# Revit family: Practibox_S_flush_mounting_cabinet_8_modules_réf_134008_to_134178
name_source: partatom
category: Equipement électrique
revit_build: Autodesk Revit 2018 (Build: 20170223_1515(x64)
units: mm (PartAtom-declared; Revit-internal decimal feet)

## family parameters
Basée sur le plan de construction = Non
Configuration du panneau = Deux colonnes, circuits au sein
Cote de connecteur circulaire = Utiliser le diamètre
Couper avec des vides une fois chargée = Non
Numéro OmniClass = 23.80.30.11.17
Partagée = Non
Point de calcul de pièce = Non
Titre OmniClass = Distribution Boards and Control Panels
Toujours verticalement = Oui
Type d'élément = Tableau de raccordement

## types (8) — shared parameters
Fabricant = "Legrand"
General Conditions of Use = https://export.legrand.com
Ina = 63 A
URL = www.legrand.com
depth = 100 mm  [stored 0.328084 ft]
height = 225 mm  [stored 0.738189 ft]
size = 8 modules
width = 184 mm  [stored 0.603675 ft]

## per-type parameters (varying)
| type | Terminal block E | Terminal block N | door transparent | door white |
| Practibox_S_flush_mounting_cabinet_8_modules_134148 | 6 connections Icc 6kA | 6 connections Icc 6kA | Non | Oui |
| Practibox_S_flush_mounting_cabinet_8_modules_134158 | 6 connections Icc 6kA | 6 connections Icc 6kA | Oui | Non |
| Practibox_S_flush_mounting_cabinet_8_modules_134008 |  |  | Non | Oui |
| Practibox_S_flush_mounting_cabinet_8_modules_134018 |  |  | Oui | Non |
| Practibox_S_flush_mounting_cabinet_8_modules_134028 |  |  | Non | Oui |
| Practibox_S_flush_mounting_cabinet_8_modules_134038 |  |  | Oui | Non |
| Practibox_S_flush_mounting_cabinet_8_modules_134168 | 6 connections Icc 6kA | 6 connections Icc 6kA | Non | Oui |
| Practibox_S_flush_mounting_cabinet_8_modules_134178 | 6 connections Icc 6kA | 6 connections Icc 6kA | Oui | Non |

note: column(s) folded — value = type name in every type: Description

note: [stored X ft] marks values corroborated as IEEE doubles in the binary element streams (Revit-internal decimal feet)
